# Revit family: ГРЕЕРС ЕС-12
name_source: partatom
category: Оборудование
revit_build: Autodesk Revit 2017 (Build: 20161006_0315(x64)
units: mm (PartAtom-declared; Revit-internal decimal feet)

## family parameters
Общий = Нет
Основа = Грань
При загрузке вырезать с полостями = Нет
Размер круглого соединителя = Использовать диаметр
Тип детали = Нормальный
Точка расчета площади = Нет

## types (1)
- ГРЕЕРС ЕС-12
    URL = https://greers.ru
    Вентилятор = Осевой, однофазный, переменного тока, с 3-х скоростным двигателем
    Вес аппарата = 26.5
    Группа модели = Электрический тепловентилятор
    Изготовитель = ООО "ЮНИО-ВЕНТ"
    Класс защиты = IP 21
    Классификация нагрузки = Нагревательный ТЭН
    Коэффициент мощности = 1
    Максимальное потребление тока = 0 А
    Максимальный расход мощности = 0 Вт
    Материал = Сталь окрашенная
    Напряжение питания = 380 В
    Номинальная тепловая мощность = 0 кВт
    Описание = ГРЕЕРС ЕС-12
    Отметка по умолчанию = 2500 мм
    Полная установленная мощность = 0 В·А
    Производительность = 0.0 л/с
    Рост температуры = 0 °C
